FCSTD DOCUMENT  (FreeCAD 0.21R33668 +26 (Git))
Label: Tuto1-003
License: All rights reserved
LicenseURL: http://en.wikipedia.org/wiki/All_rights_reserved
objects: PartDesign::CoordinateSystem×4, App::DocumentObjectGroup×3, App::Link×3, App::FeaturePython×1, Sketcher::SketchObject×1, App::Part×1
note: 5 computed .brp shape members not serialized (recipe doc carries the construction recipe); baked Part::Feature solids carry a one-line shape summary decoded from their .brp
EXTERNAL_REF file=Pieces-bielles.FCStd obj=LCS_0
EXTERNAL_REF file=Pieces-bielles.FCStd obj=Body
EXTERNAL_REF file=Pieces-bielles.FCStd obj=LCS_002
EXTERNAL_REF file=Pieces-bielles.FCStd obj=Body001
EXTERNAL_REF file=Pieces-bielles.FCStd obj=LCS_003
EXTERNAL_REF file=Pieces-bielles.FCStd obj=Plateau

FEATURE [App::DocumentObjectGroup] Parts
FEATURE [PartDesign::CoordinateSystem] LCS_Origin
  AttacherType = Attacher::AttachEngine3D
  MapMode = 2
  Support = -> [X_Axis]
FEATURE [App::DocumentObjectGroup] Constraints
FEATURE [App::FeaturePython] Variables  # WARN: FeaturePython — macro-defined, semantics opaque (R4)
  Type = App::PropertyContainer
  rotation_bielle1 = 13.13
FEATURE [App::DocumentObjectGroup] Configurations
FEATURE [Sketcher::SketchObject] Sketch_1
  FullyConstrained = true
  Support = -> [YZ_Plane]
  expr: Constraints[11] = Variables.rotation_bielle1
  sketch-geometry (3):
    g0: LineSegment StartX=133.611 StartY=2.31422 StartZ=0 EndX=83.6449 EndY=195.972 EndZ=0
    g1: LineSegment StartX=0 StartY=120 StartZ=0 EndX=97.3857 EndY=142.716 EndZ=0
    g2: LineSegment StartX=0 StartY=50 StartZ=0 EndX=119.871 EndY=55.5701 EndZ=0
  constraints (12):
    c: PointOnObject(g1,g0)
    c: PointOnObject(g2,g0)
    c: PointOnObject(g1,g-2)
    c: Distance(g1,g0) = 55
    c: Distance(g2,g0) = 55
    c: PointOnObject(g2,g-2)
    c: Distance(g2) = 120
    c: DistanceY(g-1,g1) = 120
    c: Distance(g1,g1) = 100
    c: Distance(g0) = 200
    c: DistanceY(g-1,g2) = 50
    c: Angle(g-1,g1) = 0.229162
FEATURE [PartDesign::CoordinateSystem] LCS_1
  AttacherType = Attacher::AttachEngine3D
  MapMode = 7
  Placement = pos=(0,120,0) rot=(0.665256,-0.527937,-0.527937;1.96754rad)
  Support = -> [Sketch_1]
FEATURE [PartDesign::CoordinateSystem] LCS_2
  AttacherType = Attacher::AttachEngine3D
  MapMode = 7
  Placement = pos=(133.611,2.31422,0) rot=(0.984268,0.124932,0.124932;1.58665rad)
  Support = -> [Sketch_1]
FEATURE [PartDesign::CoordinateSystem] LCS_3
  AttacherType = Attacher::AttachEngine3D
  MapMode = 7
  Placement = pos=(0,50,0) rot=(0.595221,-0.568204,-0.568204;2.0678rad)
  Support = -> [Sketch_1]
FEATURE [App::Link] Bielle_001  label="Bielle-001"
  AttachedBy = #LCS_0
  AttachedTo = Parent Assembly#LCS_1
  AttachmentOffset = pos=(0,0,0) rot=(-0.707107,0,0.707107;3.14159rad)
  LinkPlacement = pos=(0,120,0) rot=(-0.987013,-0.11359,0.11359;1.58387rad)
  LinkedObject = -> <external Pieces-bielles.FCStd>#Body
  Placement = pos=(0,120,0) rot=(-0.987013,-0.11359,0.11359;1.58387rad)
  SolverId = Asm4EE
  expr: Placement = LCS_1.Placement * AttachmentOffset * Pieces_bielles#LCS_0.Placement ^ -1
FEATURE [App::Link] Bielle_002  label="Bielle-002"
  AttachedBy = #LCS_002
  AttachedTo = Parent Assembly#LCS_3
  AttachmentOffset = pos=(0,0,0) rot=(-0.707107,0,0.707107;3.14159rad)
  LinkPlacement = pos=(0,50,0) rot=(-0.999461,-0.023209,0.023209;1.57133rad)
  LinkedObject = -> <external Pieces-bielles.FCStd>#Body001
  Placement = pos=(0,50,0) rot=(-0.999461,-0.023209,0.023209;1.57133rad)
  SolverId = Asm4EE
  expr: Placement = LCS_3.Placement * AttachmentOffset * Pieces_bielles#LCS_002.Placement ^ -1
FEATURE [App::Link] Plateau
  AttachedBy = #LCS_003
  AttachedTo = Parent Assembly#LCS_2
  AttachmentOffset = pos=(0,0,0) rot=(-0.57735,0.57735,0.57735;4.18879rad)
  LinkPlacement = pos=(133.611,2.31422,0) rot=(-0.704276,-0.089393,0.704276;3.3199rad)
  LinkedObject = -> <external Pieces-bielles.FCStd>#Plateau
  Placement = pos=(133.611,2.31422,0) rot=(-0.704276,-0.089393,0.704276;3.3199rad)
  SolverId = Asm4EE
  expr: Placement = LCS_2.Placement * AttachmentOffset * Pieces_bielles#LCS_003.Placement ^ -1
FEATURE [App::Part] Assembly
  AssemblyType = Part::Link
  Group = -> [LCS_Origin,Constraints,Variables,Configurations,Sketch_1,LCS_1,LCS_2,LCS_3,Bielle_001,Bielle_002,Plateau]
  Origin = -> Origin
  Type = Assembly

RESOLVED EXTERNAL PARTS (link-assembly join: the EXTERNAL_REF files above that resolve inside this repo's crawl, each included once):
---- part Pieces-bielles.FCStd = doc fcstd_4507086b8ff4 ----
FCSTD DOCUMENT  (FreeCAD 0.21R33668 +26 (Git))
Label: Pieces-bielles
License: All rights reserved
LicenseURL: http://en.wikipedia.org/wiki/All_rights_reserved
objects: Sketcher::SketchObject×4, PartDesign::Pad×4, PartDesign::CoordinateSystem×3, PartDesign::Body×3
note: 18 computed .brp shape members not serialized (recipe doc carries the construction recipe); baked Part::Feature solids carry a one-line shape summary decoded from their .brp

FEATURE [PartDesign::CoordinateSystem] LCS_0
  AttacherType = Attacher::AttachEngine3D
  MapMode = 2
  Support = -> [X_Axis001]
FEATURE [Sketcher::SketchObject] Sketch
  FullyConstrained = false
  MapMode = 5
  Placement = pos=(0,0,0) rot=(1,0,0;1.5708rad)
  Support = -> [XZ_Plane001]
  sketch-geometry (6):
    g0: ArcOfCircle CenterX=0 CenterY=0 CenterZ=0 NormalX=0 NormalY=0 NormalZ=1 AngleXU=0 Radius=10 StartAngle=1.5708 EndAngle=4.71239
    g1: ArcOfCircle CenterX=100 CenterY=1.1e-15 CenterZ=0 NormalX=0 NormalY=0 NormalZ=1 AngleXU=0 Radius=10 StartAngle=4.71239 EndAngle=7.85398
    g2: LineSegment StartX=-1.8e-15 StartY=-10 StartZ=0 EndX=100 EndY=-10 EndZ=0
    g3: LineSegment StartX=100 StartY=10 StartZ=0 EndX=7.958e-13 EndY=10 EndZ=0
    g4: Circle CenterX=100 CenterY=1.1e-15 CenterZ=0 NormalX=0 NormalY=0 NormalZ=1 AngleXU=0 Radius=5
    g5: Circle CenterX=0 CenterY=0.067016 CenterZ=0 NormalX=0 NormalY=0 NormalZ=1 AngleXU=0 Radius=5
  constraints (11):
    c: Tangent(g0,g2) = -1.5708
    c: Tangent(g2,g1) = -1.5708
    c: Tangent(g1,g3) = -1.5708
    c: Tangent(g3,g0) = -1.5708
    c: Equal(g0,g1)
    c: Horizontal(g2)
    c: Coincident(g0,g-1)
    c: Coincident(g4,g1)
    c: PointOnObject(g5,g-2)
    c: Radius(g5) = 5
    c: DistanceX(g5,g1) = 100
FEATURE [PartDesign::Pad] Pad
  Direction = (0,-1,-2e-16)
  Length = 10
  Length2 = 10
  Placement = pos=(0,0,0) rot=(1,0,0;1.5708rad)
  Profile = -> Sketch
  ReferenceAxis = -> Sketch [N_Axis]
  Type = 0
FEATURE [PartDesign::Body] Body  label="Bielle-001"
  Group = -> [LCS_0,Sketch,Pad]
  Origin = -> Origin001
  Placement = pos=(0,51,0) rot=(0,0,1;0rad)
  Tip = -> Pad
FEATURE [PartDesign::CoordinateSystem] LCS_002
  AttacherType = Attacher::AttachEngine3D
  MapMode = 2
  Support = -> [X_Axis002]
FEATURE [Sketcher::SketchObject] Sketch001
  FullyConstrained = false
  MapMode = 5
  Placement = pos=(0,0,0) rot=(1,0,0;1.5708rad)
  Support = -> [XZ_Plane002]
  sketch-geometry (6):
    g0: ArcOfCircle CenterX=0 CenterY=0 CenterZ=0 NormalX=0 NormalY=0 NormalZ=1 AngleXU=0 Radius=9.9695 StartAngle=1.5708 EndAngle=4.71239
    g1: ArcOfCircle CenterX=120 CenterY=8e-16 CenterZ=0 NormalX=0 NormalY=0 NormalZ=1 AngleXU=0 Radius=9.9695 StartAngle=4.71239 EndAngle=7.85398
    g2: LineSegment StartX=-1.8e-15 StartY=-9.9695 StartZ=0 EndX=120 EndY=-9.9695 EndZ=0
    g3: LineSegment StartX=120 StartY=9.9695 StartZ=0 EndX=0 EndY=9.9695 EndZ=0
    g4: Circle CenterX=120 CenterY=8e-16 CenterZ=0 NormalX=0 NormalY=0 NormalZ=1 AngleXU=0 Radius=5
    g5: Circle CenterX=0 CenterY=0.067016 CenterZ=0 NormalX=0 NormalY=0 NormalZ=1 AngleXU=0 Radius=5
  constraints (11):
    c: Tangent(g0,g2) = -1.5708
    c: Tangent(g2,g1) = -1.5708
    c: Tangent(g1,g3) = -1.5708
    c: Tangent(g3,g0) = -1.5708
    c: Equal(g0,g1)
    c: Horizontal(g2)
    c: Coincident(g0,g-1)
    c: Coincident(g4,g1)
    c: PointOnObject(g5,g-2)
    c: Radius(g5) = 5
    c: DistanceX(g5,g1) = 120
FEATURE [PartDesign::Pad] Pad001
  Direction = (0,-1,-2e-16)
  Length = 10
  Length2 = 10
  Placement = pos=(0,0,0) rot=(1,0,0;1.5708rad)
  Profile = -> Sketch001
  ReferenceAxis = -> Sketch001 [N_Axis]
  Type = 0
FEATURE [PartDesign::Body] Body001  label="Bielle-002"
  Group = -> [LCS_002,Sketch001,Pad001]
  Origin = -> Origin002
  Tip = -> Pad001
FEATURE [PartDesign::CoordinateSystem] LCS_003
  AttacherType = Attacher::AttachEngine3D
  MapMode = 2
  Support = -> [X_Axis]
FEATURE [Sketcher::SketchObject] Sketch002
  FullyConstrained = true
  MapMode = 5
  Placement = pos=(0,0,0) rot=(0.57735,0.57735,0.57735;2.0944rad)
  Support = -> [YZ_Plane]
  sketch-geometry (4):
    g0: LineSegment StartX=-200 StartY=13 StartZ=0 EndX=0 EndY=13 EndZ=0
    g1: LineSegment StartX=0 StartY=13 StartZ=0 EndX=-3.6e-15 EndY=-13 EndZ=0
    g2: LineSegment StartX=-3.6e-15 StartY=-13 StartZ=0 EndX=-200 EndY=-13 EndZ=0
    g3: LineSegment StartX=-200 StartY=-13 StartZ=0 EndX=-200 EndY=13 EndZ=0
  constraints (11):
    c: Coincident(g0,g1)
    c: Coincident(g1,g2)
    c: Coincident(g2,g3)
    c: Coincident(g3,g0)
    c: Horizontal(g0)
    c: Horizontal(g2)
    c: Vertical(g3)
    c: Distance(g0,g0) = 200
    c: Distance(g0,g2) = 26
    c: Symmetric(g0,g1,g-1)
    c: PointOnObject(g0,g-2)
FEATURE [PartDesign::Pad] Pad002
  Direction = (1,-2e-16,3e-16)
  Length = 100
  Length2 = 10
  Placement = pos=(0,0,0) rot=(1,1,1;2.0944rad)
  Profile = -> Sketch002
  ReferenceAxis = -> Sketch002 [N_Axis]
  Type = 0
FEATURE [Sketcher::SketchObject] Sketch003
  ExternalGeometry = -> [Pad002]
  FullyConstrained = true
  MapMode = 5
  Placement = pos=(0,0,0) rot=(0.57735,0.57735,0.57735;2.0944rad)
  Support = -> [YZ_Plane]
  sketch-geometry (2):
    g0: Circle CenterX=-55 CenterY=0 CenterZ=0 NormalX=0 NormalY=0 NormalZ=1 AngleXU=0 Radius=4.8
    g1: Circle CenterX=-145.4 CenterY=0 CenterZ=0 NormalX=0 NormalY=0 NormalZ=1 AngleXU=0 Radius=4.8
  constraints (6):
    c: PointOnObject(g0,g-1)
    c: Radius(g0) = 4.8
    c: Distance(g-1,g0) = 55
    c: PointOnObject(g1,g-1)
    c: Radius(g1) = 4.8
    c: Distance(g0,g1) = 90.4
FEATURE [PartDesign::Pad] Pad003
  BaseFeature = -> Pad002
  Direction = (1,-2e-16,3e-16)
  Length = 12
  Length2 = 10
  Placement = pos=(0,0,0) rot=(1,1,1;2.0944rad)
  Profile = -> Sketch003
  ReferenceAxis = -> Sketch003 [N_Axis]
  Reversed = true
  Type = 0
FEATURE [PartDesign::Body] Plateau
  Group = -> [LCS_003,Sketch002,Pad002,Sketch003,Pad003]
  Origin = -> Origin
  Placement = pos=(0,-45,0) rot=(0,0,1;0rad)
  Tip = -> Pad003
